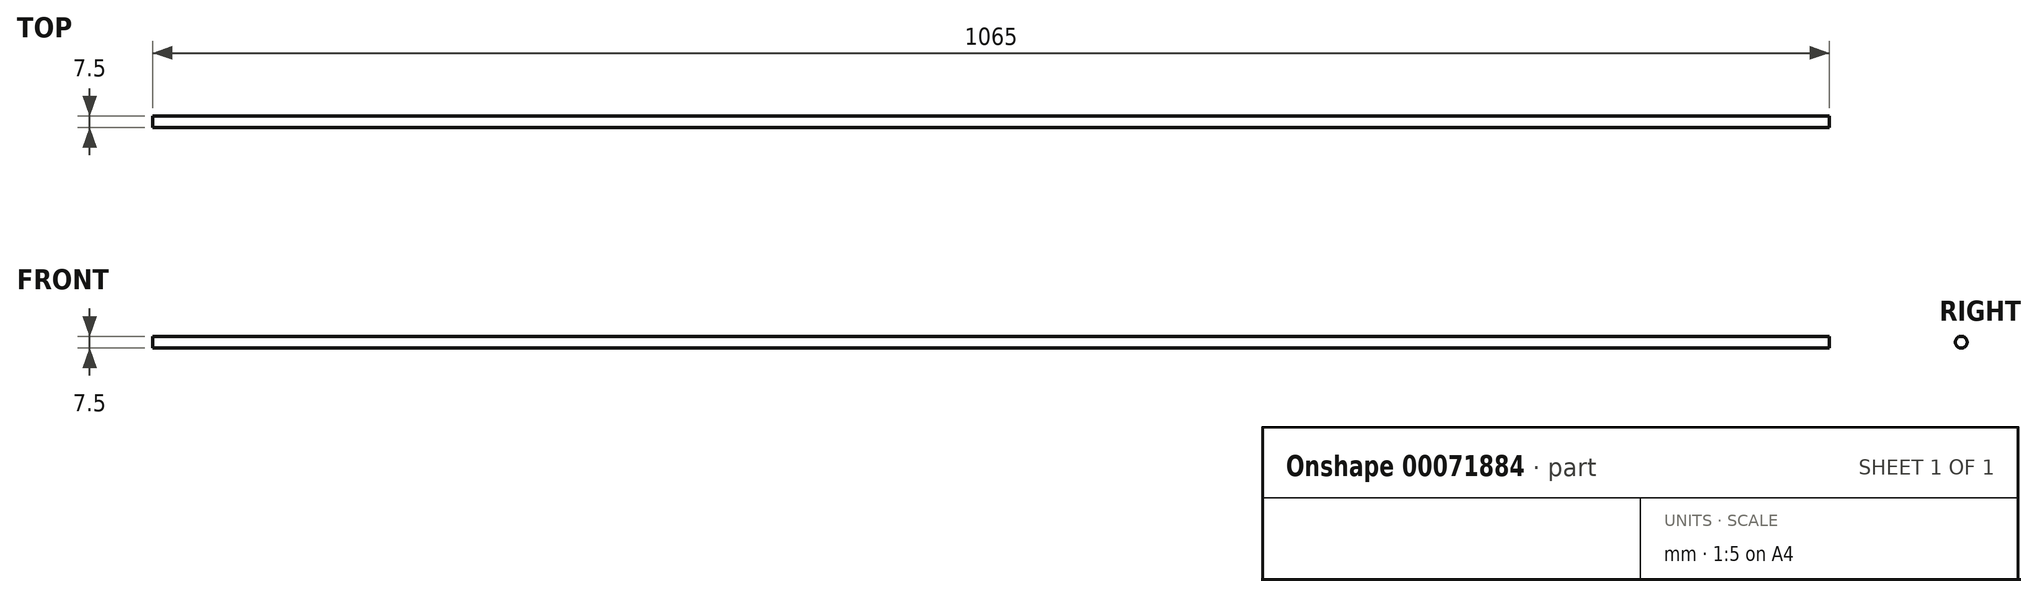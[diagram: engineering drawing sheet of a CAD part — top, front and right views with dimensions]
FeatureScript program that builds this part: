
annotation { "Feature Type Name" : "Feature", "Feature Type Description" : "" }
export const myFeature = defineFeature(function(context is Context, id is Id, definition is map)
    precondition{}
    {
        {
            var Q0;
            Q0=qCreatedBy(makeId("Right.planeOp"),FACE);
            var sketch = newSketch(context, id + "F0", { "sketchPlane" : qUnion([Q0])});
            skCircle(sketch, "E0", {"center": v(0, 0) * mm, "radius": 3.75 * mm});
            skSolve(sketch);
        }
        {
            var Q0;
            Q0=makeQuery(id+"F0.imprint","IMPRINT",FACE,{"disambiguationData":[TD([[makeQuery(id+"F0.imprint","IMPRINT",EDGE,{"derivedFrom":sQuery(id+"F0.wireOp",EDGE,"E0")}),1.0]])]});
            extrude(context, id + "F1", {"entities" : qUnion([Q0]), "depth" : 1065 * mm});
        }
    });
